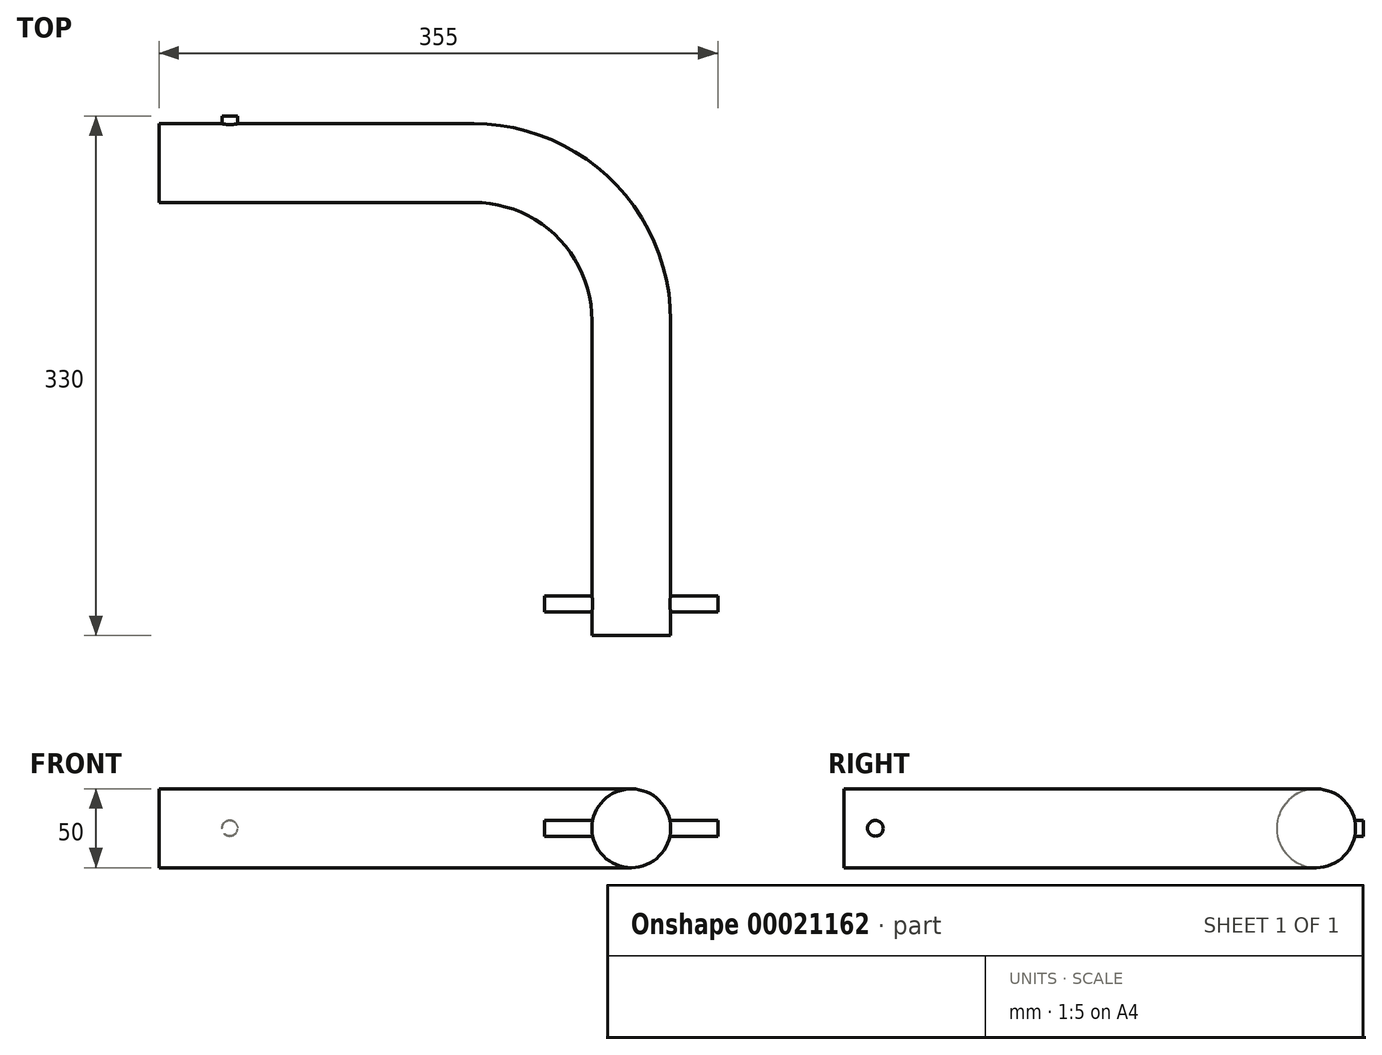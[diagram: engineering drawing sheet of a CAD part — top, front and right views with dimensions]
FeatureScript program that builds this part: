
annotation { "Feature Type Name" : "Feature", "Feature Type Description" : "" }
export const myFeature = defineFeature(function(context is Context, id is Id, definition is map)
    precondition{}
    {
        {
            var Q0;
            Q0=qCreatedBy(makeId("Top.planeOp"),FACE);
            var sketch = newSketch(context, id + "F0", { "sketchPlane" : qUnion([Q0])});
            skLineSegment(sketch, "E0", {"start": v(0, 0) * mm, "end": v(0, 200) * mm});
            skLineSegment(sketch, "E1", {"start": v(-100, 300) * mm, "end": v(-300, 300) * mm});
            skPoint(sketch, "E2.visualSharp", {"position": v(0, 300) * mm});
            skArc(sketch, "E2.filletArc", {"start": v(0, 200) * mm, "mid": v(-29.29, 270.71) * mm, "end": v(-100, 300) * mm});
            skSolve(sketch);
        }
        {
            var Q0;
            Q0=qCreatedBy(makeId("Front.planeOp"),FACE);
            var sketch = newSketch(context, id + "F1", { "sketchPlane" : qUnion([Q0])});
            skCircle(sketch, "E3", {"center": v(0, 0) * mm, "radius": 25 * mm});
            skSolve(sketch);
        }
        {
            var Q0;
            Q0=makeQuery(id+"F1.imprint","IMPRINT",FACE,{"disambiguationData":[TD([[makeQuery(id+"F1.imprint","IMPRINT",EDGE,{"derivedFrom":sQuery(id+"F1.wireOp",EDGE,"E3")}),1.0]])]});
            var Q1;
            Q1=sQuery(id+"F0.wireOp",EDGE,"E0");
            var Q2;
            Q2=sQuery(id+"F0.wireOp",EDGE,"E2.filletArc");
            var Q3;
            Q3=sQuery(id+"F0.wireOp",EDGE,"E1");
            sweep(context, id + "F2", {"profiles" : qUnion([Q0]), "path" : qUnion([Q1, Q2, Q3])});
        }
        {
            var Q0;
            Q0=qCreatedBy(makeId("Right.planeOp"),FACE);
            var sketch = newSketch(context, id + "F3", { "sketchPlane" : qUnion([Q0])});
            skCircle(sketch, "E4", {"center": v(20, 0) * mm, "radius": 5 * mm});
            skSolve(sketch);
        }
        {
            var Q0;
            Q0=qSketchRegion(id+"F3",true);
            extrude(context, id + "F4", {"entities" : qUnion([Q0]), "operationType" : NewBodyOperationType.ADD, "endBound" : BoundingType.SYMMETRIC, "depth" : 110 * mm});
        }
        {
            var Q0;
            Q0=makeQuery(id+"F2.opSweep","CAP_FACE",FACE,{"disambiguationData":[OSD([sQuery(id+"F0.wireOp",VERTEX,"E0.start"),sQuery(id+"F1.wireOp",EDGE,"E3")])],"isStart":true});
            cPlane(context, id + "F5", {"entities" : qUnion([Q0]), "cplaneType" : CPlaneType.OFFSET, "offset" : (300 + 30) * mm, "oppositeDirection" : true, "width" : 150 * mm, "height" : 150 * mm});
        }
        {
            var Q0;
            Q0=qCreatedBy(id+"F5.planeOp",FACE);
            var sketch = newSketch(context, id + "F6", { "sketchPlane" : qUnion([Q0])});
            skCircle(sketch, "E5", {"center": v(-255, 0) * mm, "radius": 5 * mm});
            skSolve(sketch);
        }
        {
            var Q0;
            Q0=makeQuery(id+"F6.imprint","IMPRINT",FACE,{"disambiguationData":[TD([[makeQuery(id+"F6.imprint","IMPRINT",EDGE,{"derivedFrom":sQuery(id+"F6.wireOp",EDGE,"E5")}),1.0]])]});
            extrude(context, id + "F7", {"entities" : qUnion([Q0]), "operationType" : NewBodyOperationType.ADD, "endBound" : BoundingType.UP_TO_NEXT, "depth" : 25 * mm});
        }
    });
